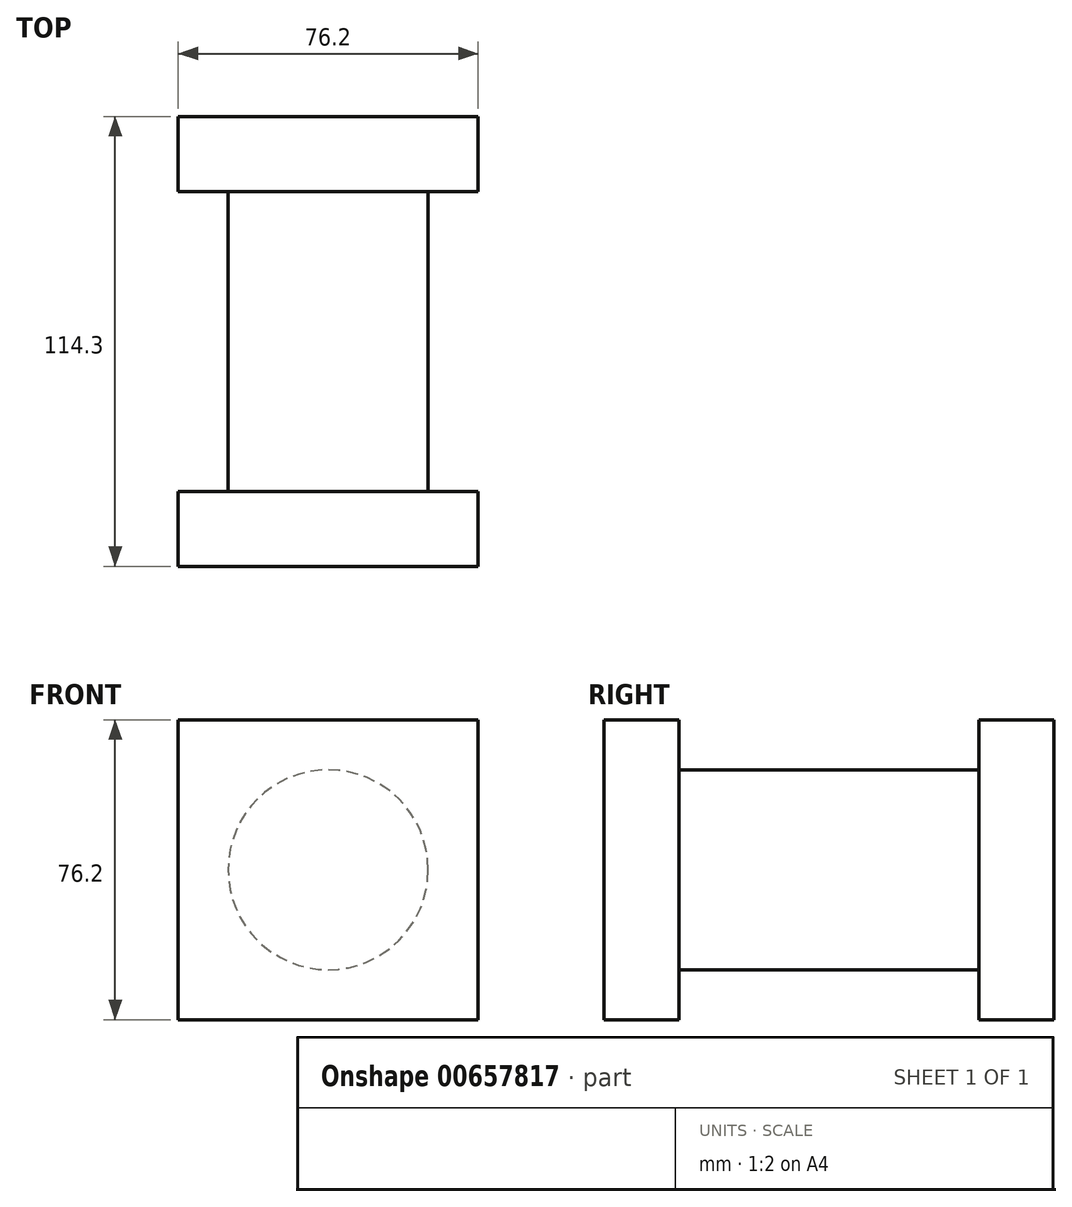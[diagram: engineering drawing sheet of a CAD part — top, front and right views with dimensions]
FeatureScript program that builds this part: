
annotation { "Feature Type Name" : "Feature", "Feature Type Description" : "" }
export const myFeature = defineFeature(function(context is Context, id is Id, definition is map)
    precondition{}
    {
        {
            var Q0;
            Q0=qCreatedBy(makeId("Front.planeOp"),FACE);
            var sketch = newSketch(context, id + "F0", { "sketchPlane" : qUnion([Q0])});
            skLineSegment(sketch, "E0.bottom", {"start": v(38.1, -38.1) * mm, "end": v(-38.1, -38.1) * mm});
            skLineSegment(sketch, "E0.top", {"start": v(38.1, 38.1) * mm, "end": v(-38.1, 38.1) * mm});
            skLineSegment(sketch, "E0.left", {"start": v(38.1, -38.1) * mm, "end": v(38.1, 38.1) * mm});
            skLineSegment(sketch, "E0.right", {"start": v(-38.1, -38.1) * mm, "end": v(-38.1, 38.1) * mm});
            skPoint(sketch, "E0.middle", {"position": v(0, 0) * mm});
            skSolve(sketch);
        }
        {
            var Q0;
            Q0=makeQuery(id+"F0.imprint","IMPRINT",FACE,{"disambiguationData":[TD([[makeQuery(id+"F0.imprint","IMPRINT",EDGE,{"derivedFrom":sQuery(id+"F0.wireOp",EDGE,"E0.bottom")}),-1.0]])]});
            extrude(context, id + "F1", {"entities" : qUnion([Q0]), "depth" : 19.05 * mm, "offsetDistance" : 25.4 * mm});
        }
        {
            var Q0;
            Q0=makeQuery(id+"F1.opExtrude","CAP_FACE",FACE,{"disambiguationData":[OSD([sQuery(id+"F0.wireOp",EDGE,"E0.bottom"),sQuery(id+"F0.wireOp",EDGE,"E0.top"),sQuery(id+"F0.wireOp",EDGE,"E0.left"),sQuery(id+"F0.wireOp",EDGE,"E0.right")])],"isStart":false});
            var sketch = newSketch(context, id + "F2", { "sketchPlane" : qUnion([Q0])});
            skCircle(sketch, "E1", {"center": v(0, 0) * mm, "radius": 25.4 * mm});
            skSolve(sketch);
        }
        {
            var Q0;
            Q0=makeQuery(id+"F2.imprint","IMPRINT",FACE,{"disambiguationData":[TD([[makeQuery(id+"F2.imprint","IMPRINT",EDGE,{"derivedFrom":sQuery(id+"F2.wireOp",EDGE,"E1")}),1.0]])]});
            extrude(context, id + "F3", {"entities" : qUnion([Q0]), "operationType" : NewBodyOperationType.ADD, "depth" : 76.2 * mm, "offsetDistance" : 25.4 * mm});
        }
        {
            var Q0;
            Q0=makeQuery(id+"F3.opExtrude","CAP_FACE",FACE,{"disambiguationData":[OSD([sQuery(id+"F2.wireOp",EDGE,"E1")])],"isStart":false});
            var sketch = newSketch(context, id + "F4", { "sketchPlane" : qUnion([Q0])});
            skLineSegment(sketch, "E2.bottom", {"start": v(-39.2, -38.1) * mm, "end": v(39.2, -38.1) * mm});
            skLineSegment(sketch, "E2.top", {"start": v(-39.2, 38.1) * mm, "end": v(39.2, 38.1) * mm});
            skLineSegment(sketch, "E2.left", {"start": v(-39.2, -38.1) * mm, "end": v(-39.2, 38.1) * mm});
            skLineSegment(sketch, "E2.right", {"start": v(39.2, -38.1) * mm, "end": v(39.2, 38.1) * mm});
            skPoint(sketch, "E2.middle", {"position": v(0, 0) * mm});
            skSolve(sketch);
        }
        {
            var Q0;
            Q0=makeQuery(id+"F4.imprint","IMPRINT",FACE,{"disambiguationData":[TD([[makeQuery(id+"F4.imprint","IMPRINT",EDGE,{"derivedFrom":sQuery(id+"F4.wireOp",EDGE,"E2.bottom")}),1.0]])]});
            extrude(context, id + "F5", {"entities" : qUnion([Q0]), "depth" : 19.05 * mm, "offsetDistance" : 25.4 * mm});
        }
        {
            var Q0;
            Q0=makeQuery(id+"F5.opExtrude","SWEPT_BODY",BODY,{"disambiguationData":[OSD([sQuery(id+"F2.wireOp",EDGE,"E1"),sQuery(id+"F4.wireOp",EDGE,"E2.bottom"),sQuery(id+"F4.wireOp",EDGE,"E2.top"),sQuery(id+"F4.wireOp",EDGE,"E2.left"),sQuery(id+"F4.wireOp",EDGE,"E2.right")])]});
            deleteBodies(context, id + "F6", {"entities" : qUnion([Q0])});
        }
        {
            var Q0;
            Q0=makeQuery(id+"F3.opExtrude","CAP_FACE",FACE,{"disambiguationData":[OSD([sQuery(id+"F2.wireOp",EDGE,"E1")])],"isStart":false});
            var sketch = newSketch(context, id + "F7", { "sketchPlane" : qUnion([Q0])});
            skLineSegment(sketch, "E3.bottom", {"start": v(38.1, -38.1) * mm, "end": v(-38.1, -38.1) * mm});
            skLineSegment(sketch, "E3.top", {"start": v(38.1, 38.1) * mm, "end": v(-38.1, 38.1) * mm});
            skLineSegment(sketch, "E3.left", {"start": v(38.1, -38.1) * mm, "end": v(38.1, 38.1) * mm});
            skLineSegment(sketch, "E3.right", {"start": v(-38.1, -38.1) * mm, "end": v(-38.1, 38.1) * mm});
            skPoint(sketch, "E3.middle", {"position": v(0, 0) * mm});
            skSolve(sketch);
        }
        {
            var Q0;
            Q0=makeQuery(id+"F7.imprint","IMPRINT",FACE,{"disambiguationData":[TD([[makeQuery(id+"F7.imprint","IMPRINT",EDGE,{"derivedFrom":makeQuery(id+"F3.opExtrude","CAP_EDGE",EDGE,{"disambiguationData":[OSD([sQuery(id+"F2.wireOp",EDGE,"E1")])],"isStart":false})}),1.0]])]});
            var Q1;
            Q1=makeQuery(id+"F7.imprint","IMPRINT",FACE,{"disambiguationData":[TD([[makeQuery(id+"F7.imprint","IMPRINT",EDGE,{"derivedFrom":sQuery(id+"F7.wireOp",EDGE,"E3.bottom")}),-1.0]])]});
            extrude(context, id + "F8", {"entities" : qUnion([Q0, Q1]), "operationType" : NewBodyOperationType.ADD, "depth" : 19.05 * mm, "offsetDistance" : 25.4 * mm});
        }
    });
